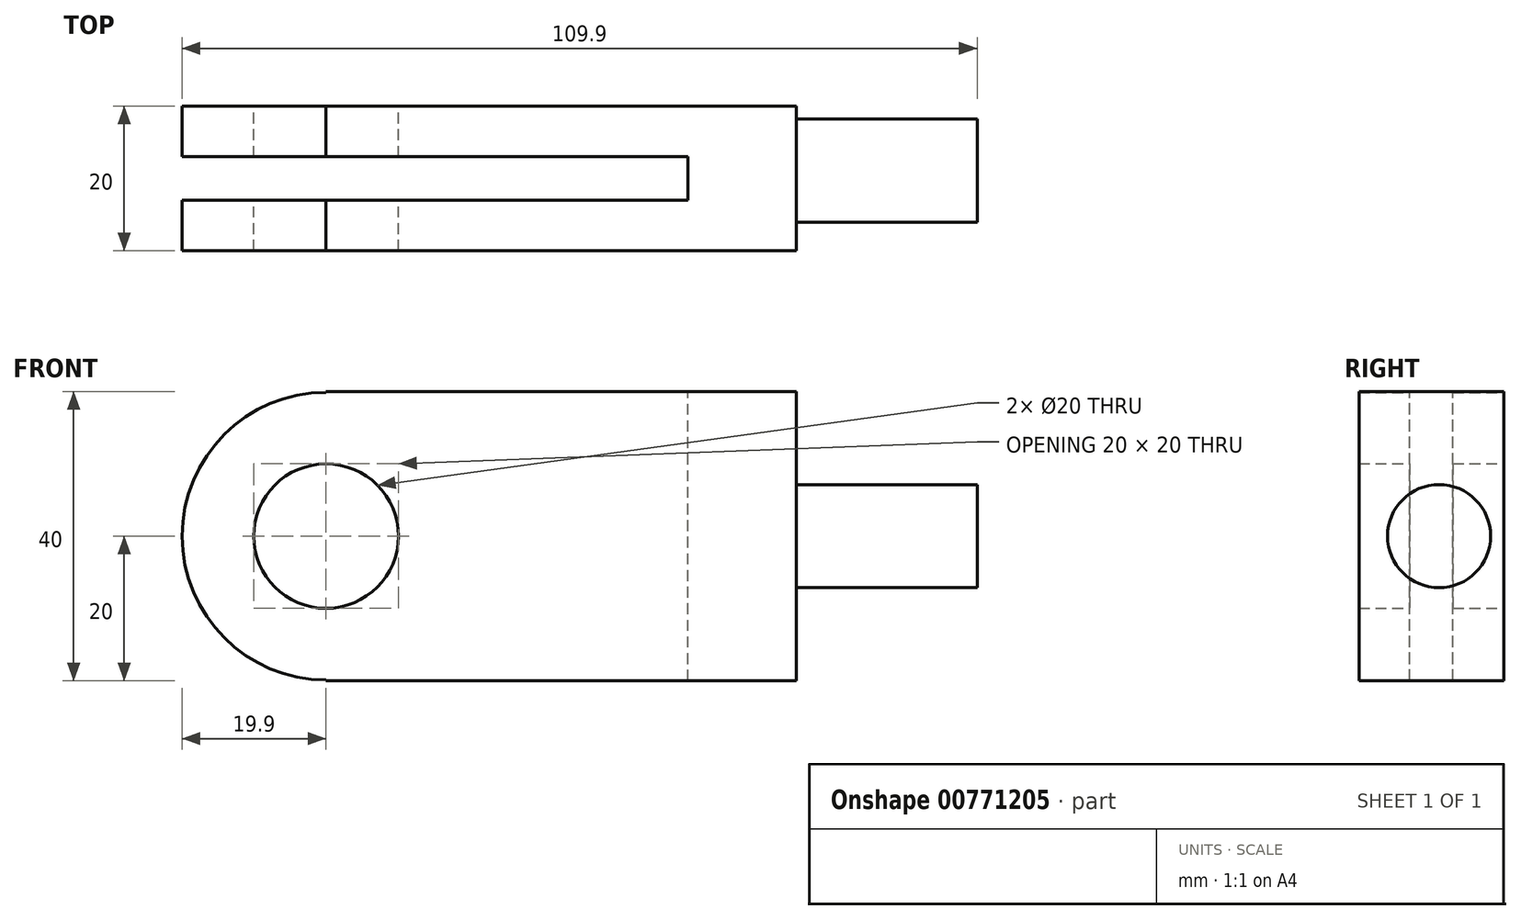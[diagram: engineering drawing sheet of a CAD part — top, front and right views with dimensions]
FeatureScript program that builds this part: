
annotation { "Feature Type Name" : "Feature", "Feature Type Description" : "" }
export const myFeature = defineFeature(function(context is Context, id is Id, definition is map)
    precondition{}
    {
        {
            var Q0;
            Q0=qCreatedBy(makeId("Front.planeOp"),FACE);
            var sketch = newSketch(context, id + "F0", { "sketchPlane" : qUnion([Q0])});
            skLineSegment(sketch, "E0.bottom", {"start": v(0, 0) * mm, "end": v(-65, 0) * mm});
            skLineSegment(sketch, "E0.top", {"start": v(0, 40) * mm, "end": v(-65, 40) * mm});
            skLineSegment(sketch, "E0.left", {"start": v(0, 0) * mm, "end": v(0, 40) * mm});
            skLineSegment(sketch, "E0.right", {"start": v(-65, 0) * mm, "end": v(-65, 0.1) * mm});
            skArc(sketch, "E1", {"start": v(-65, 39.9) * mm, "mid": v(-84.9, 20) * mm, "end": v(-65, 0.1) * mm});
            skLineSegment(sketch, "E2.trimOffspring", {"start": v(-65, 39.9) * mm, "end": v(-65, 40) * mm});
            skCircle(sketch, "E3", {"center": v(-65, 20) * mm, "radius": 10 * mm});
            skSolve(sketch);
        }
        {
            var Q0;
            Q0 = qSketchRegion(id + "F0", true);
            extrude(context, id + "F1", {"entities" : qUnion([Q0]), "depth" : 20 * mm, "offsetDistance" : 25 * mm});
        }
        {
            var Q0;
            Q0=makeQuery(id+"F1.opExtrude","SWEPT_FACE",FACE,{"disambiguationData":[OSD([sQuery(id+"F0.wireOp",EDGE,"E0.top")])]});
            var sketch = newSketch(context, id + "F2", { "sketchPlane" : qUnion([Q0])});
            skLineSegment(sketch, "E4", {"start": v(-15, -7) * mm, "end": v(-89.5, -7) * mm});
            skLineSegment(sketch, "E5", {"start": v(-15, -13) * mm, "end": v(-89.5, -13) * mm});
            skLineSegment(sketch, "E6", {"start": v(-89.5, -13) * mm, "end": v(-89.5, -7) * mm});
            skLineSegment(sketch, "E7", {"start": v(-15, -13) * mm, "end": v(-15, -7) * mm});
            skSolve(sketch);
        }
        {
            var Q0;
            Q0 = qSketchRegion(id + "F2", true);
            extrude(context, id + "F3", {"entities" : qUnion([Q0]), "operationType" : NewBodyOperationType.REMOVE, "endBound" : BoundingType.UP_TO_NEXT, "oppositeDirection" : true, "depth" : 25 * mm, "offsetDistance" : 25 * mm});
        }
        {
            var Q0;
            Q0=makeQuery(id+"F1.opExtrude","SWEPT_FACE",FACE,{"disambiguationData":[OSD([sQuery(id+"F0.wireOp",EDGE,"E0.left")])]});
            var sketch = newSketch(context, id + "F4", { "sketchPlane" : qUnion([Q0])});
            skCircle(sketch, "E8", {"center": v(-8.92, 20) * mm, "radius": 7.13 * mm});
            skPoint(sketch, "E8.centerSnap0", {"position": v(-20, 20) * mm});
            skSolve(sketch);
        }
        {
            var Q0;
            Q0 = qSketchRegion(id + "F4", true);
            extrude(context, id + "F5", {"entities" : qUnion([Q0]), "operationType" : NewBodyOperationType.ADD, "depth" : 25 * mm, "offsetDistance" : 25 * mm});
        }
    });
